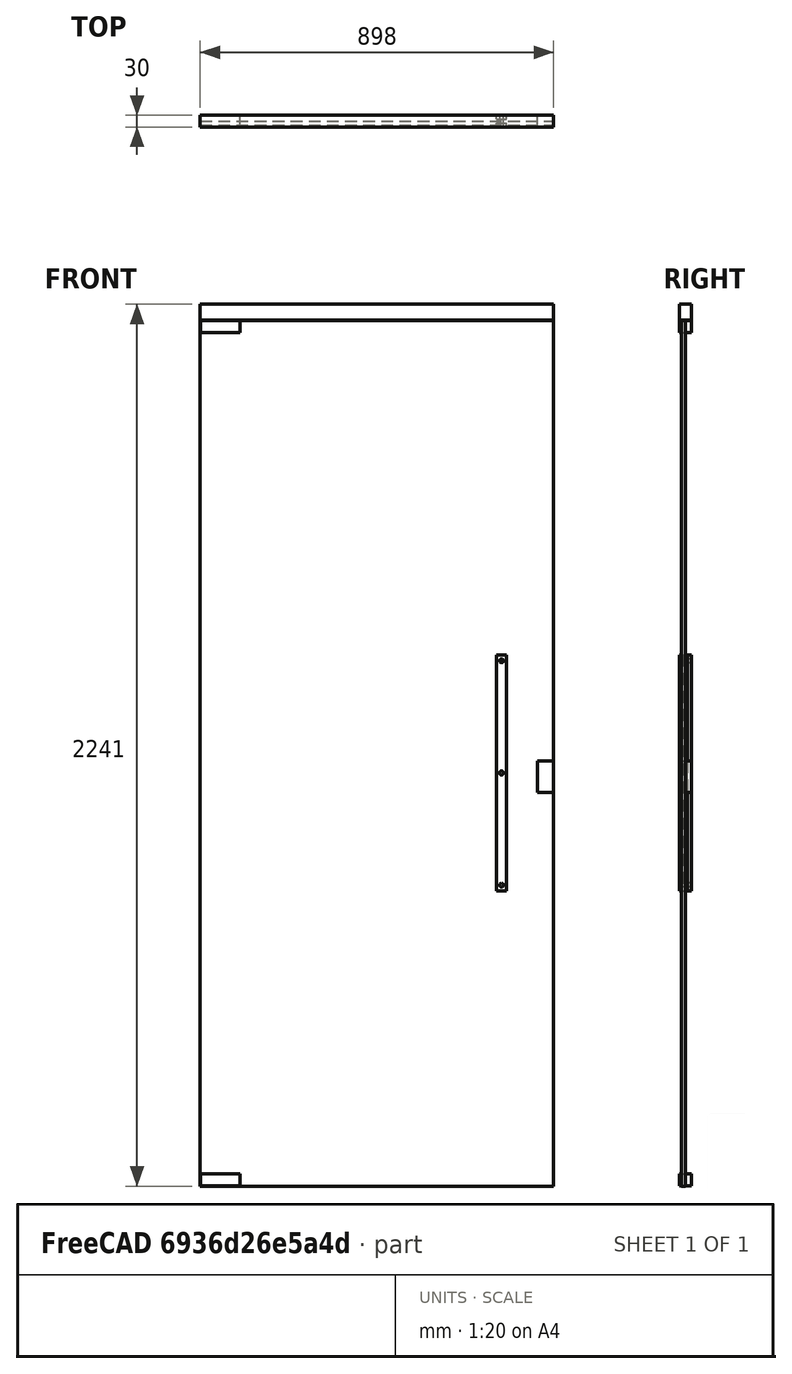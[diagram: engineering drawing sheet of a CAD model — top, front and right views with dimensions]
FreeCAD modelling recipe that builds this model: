
FCSTD DOCUMENT  (FreeCAD 0.16R6704 (Git))
Label: Simple glass door with lintel and handles
License: CreativeCommons Attribution
LicenseURL: http://creativecommons.org/licenses/by/4.0/
objects: Sketcher::SketchObject×2, Part::FeaturePython×1, App::DocumentObjectGroup×1
note: 3 computed .brp shape members not serialized (recipe doc carries the construction recipe); baked Part::Feature solids carry a one-line shape summary decoded from their .brp

FEATURE [Sketcher::SketchObject] Sketch133
  Placement = pos=(0,0,0) rot=(1,0,0;1.5708rad)
  sketch-geometry (37):
    g0: LineSegment StartX=0 StartY=0 StartZ=0 EndX=900 EndY=0 EndZ=0
    g1: LineSegment StartX=900 StartY=2242 StartZ=0 EndX=0 EndY=2242 EndZ=0
    g2: LineSegment StartX=0 StartY=2242 StartZ=0 EndX=0 EndY=0 EndZ=0
    g3: LineSegment StartX=1 StartY=0 StartZ=0 EndX=899 EndY=0 EndZ=0
    g4: LineSegment StartX=899 StartY=0 StartZ=0 EndX=899 EndY=2200 EndZ=0
    g5: LineSegment StartX=899 StartY=2200 StartZ=0 EndX=1 EndY=2200 EndZ=0
    g6: LineSegment StartX=1 StartY=2200 StartZ=0 EndX=1 EndY=0 EndZ=0
    g7: LineSegment StartX=2 StartY=2199 StartZ=0 EndX=102 EndY=2199 EndZ=0
    g8: LineSegment StartX=102 StartY=2199 StartZ=0 EndX=102 EndY=2169 EndZ=0
    g9: LineSegment StartX=102 StartY=2169 StartZ=0 EndX=2 EndY=2169 EndZ=0
    g10: LineSegment StartX=2 StartY=2169 StartZ=0 EndX=2 EndY=2199 EndZ=0
    g11: LineSegment StartX=2 StartY=1 StartZ=0 EndX=102 EndY=1 EndZ=0
    g12: LineSegment StartX=102 StartY=1 StartZ=0 EndX=102 EndY=31 EndZ=0
    g13: LineSegment StartX=102 StartY=31 StartZ=0 EndX=2 EndY=31 EndZ=0
    g14: LineSegment StartX=2 StartY=31 StartZ=0 EndX=2 EndY=1 EndZ=0
    g15: LineSegment StartX=858 StartY=1080 StartZ=0 EndX=898 EndY=1080 EndZ=0
    g16: LineSegment StartX=898 StartY=1080 StartZ=0 EndX=898 EndY=1000 EndZ=0
    g17: LineSegment StartX=898 StartY=1000 StartZ=0 EndX=858 EndY=1000 EndZ=0
    g18: LineSegment StartX=858 StartY=1000 StartZ=0 EndX=858 EndY=1080 EndZ=0
    g19: LineSegment StartX=754 StartY=1350 StartZ=0 EndX=779 EndY=1350 EndZ=0
    g20: LineSegment StartX=779 StartY=1350 StartZ=0 EndX=779 EndY=750 EndZ=0
    g21: LineSegment StartX=779 StartY=750 StartZ=0 EndX=754 EndY=750 EndZ=0
    g22: LineSegment StartX=754 StartY=750 StartZ=0 EndX=754 EndY=1350 EndZ=0
    g23: LineSegment [constr] StartX=766.5 StartY=1473.28 StartZ=0 EndX=766.5 EndY=706.642 EndZ=0
    g24: Circle CenterX=766.5 CenterY=1335 CenterZ=0 NormalX=0 NormalY=0 NormalZ=1 Radius=5
    g25: Circle CenterX=766.5 CenterY=1050 CenterZ=0 NormalX=0 NormalY=0 NormalZ=1 Radius=5
    g26: Circle CenterX=766.5 CenterY=765 CenterZ=0 NormalX=0 NormalY=0 NormalZ=1 Radius=5
    g27: LineSegment [constr] StartX=712 StartY=1050 StartZ=0 EndX=790 EndY=1050 EndZ=0
    g28: LineSegment StartX=900 StartY=2242 StartZ=0 EndX=900 EndY=0 EndZ=0
    g29: LineSegment StartX=-0.1 StartY=2243 StartZ=0 EndX=901 EndY=2243 EndZ=0
    g30: LineSegment StartX=901 StartY=2243 StartZ=0 EndX=901 EndY=0 EndZ=0
    g31: LineSegment StartX=901 StartY=0 StartZ=0 EndX=-0.1 EndY=0 EndZ=0
    g32: LineSegment StartX=-0.1 StartY=0 StartZ=0 EndX=-0.1 EndY=2243 EndZ=0
    g33: LineSegment StartX=1 StartY=2241 StartZ=0 EndX=899 EndY=2241 EndZ=0
    g34: LineSegment StartX=899 StartY=2241 StartZ=0 EndX=899 EndY=2201 EndZ=0
    g35: LineSegment StartX=899 StartY=2201 StartZ=0 EndX=1 EndY=2201 EndZ=0
    g36: LineSegment StartX=1 StartY=2201 StartZ=0 EndX=1 EndY=2241 EndZ=0
  constraints (107):
    c: Coincident(g1,g2)
    c: Coincident(g2,g0)
    c: Horizontal(g0)
    c: Horizontal(g1)
    c: Vertical(g2)
    c: Coincident(g3,g4)
    c: Coincident(g4,g5)
    c: Coincident(g5,g6)
    c: Coincident(g6,g3)
    c: Horizontal(g3)
    c: Horizontal(g5)
    c: Vertical(g4)
    c: Vertical(g6)
    c: DistanceX(g0) = 900  'Largura do vão'
    c: DistanceX(g1,g5) = 1
    c: DistanceX(g3,g0) = 1
    c: DistanceY(g0,g3) = 0
    c: Coincident(g0,g-1)
    c: Coincident(g7,g8)
    c: Coincident(g8,g9)
    c: Coincident(g9,g10)
    c: Coincident(g10,g7)
    c: Horizontal(g7)
    c: Horizontal(g9)
    c: Vertical(g8)
    c: Vertical(g10)
    c: Coincident(g11,g12)
    c: Coincident(g12,g13)
    c: Coincident(g13,g14)
    c: Coincident(g14,g11)
    c: Horizontal(g11)
    c: Horizontal(g13)
    c: Vertical(g12)
    c: Vertical(g14)
    c: Coincident(g15,g16)
    c: Coincident(g16,g17)
    c: Coincident(g17,g18)
    c: Coincident(g18,g15)
    c: Horizontal(g15)
    c: Horizontal(g17)
    c: Vertical(g16)
    c: Vertical(g18)
    c: DistanceX(g5,g7) = 1
    c: DistanceY(g8,g7) = 30  'Altura do apoio'
    c: DistanceX(g9,g8) = 100  'Largura do apoio'
    c: Equal(g8,g12)
    c: Equal(g13,g7)
    c: DistanceX(g3,g11) = 1
    c: DistanceY(g3,g11) = 1
    c: DistanceX(g16,g3) = 1
    c: DistanceY(g17,g15) = 80  'Altura da tranca'
    c: DistanceX(g15,g15) = 40  'Largura da tranca'
    c: DistanceY(g3,g17) = 1000  'Altura da tranca ao chão'
    c: Coincident(g19,g20)
    c: Coincident(g20,g21)
    c: Coincident(g21,g22)
    c: Coincident(g22,g19)
    c: Horizontal(g19)
    c: Horizontal(g21)
    c: Vertical(g20)
    c: Vertical(g22)
    c: DistanceX(g19,g19) = 25  'Largura puxador'
    c: DistanceY(g20,g19) = 600  'Altura do puxador'
    c: Vertical(g23)  'Constraint69'
    c: Symmetric(g19,g19,g23)  'Constraint68'
    c: PointOnObject(g24,g23)  'Constraint72'
    c: PointOnObject(g25,g23)  'Constraint71'
    c: PointOnObject(g26,g23)  'Constraint70'
    c: Radius(g26) = 5  'Apoio puxador'
    c: Equal(g26,g25)  'Constraint83'
    c: Equal(g26,g24)  'Constraint82'
    c: DistanceY(g24,g19) = 15  'Constraint73'
    c: DistanceY(g20,g26) = 15
    c: Horizontal(g27)
    c: PointOnObject(g25,g27)
    c: Symmetric(g21,g19,g27)
    c: DistanceY(g3,g20) = 750  'Distância do puxador ao solo'
    c: DistanceX(g20,g3) = 120  'Distância do puxador'
    c: Coincident(g28,g1)  'Constraint79'
    c: Coincident(g28,g0)
    c: Vertical(g28)
    c: DistanceY(g-1,g5) = 2200  'Altura da porta'
    c: Coincident(g29,g30)  'Constraint93'
    c: Coincident(g30,g31)  'Constraint92'
    c: Coincident(g31,g32)  'Constraint91'
    c: Coincident(g32,g29)
    c: Horizontal(g29)
    c: Horizontal(g31)
    c: Vertical(g30)
    c: Vertical(g32)
    c: DistanceX(g29,g1) = 0.1
    c: DistanceY(g1,g29) = 1
    c: DistanceX(g1,g29) = 1
    c: DistanceY(g31,g-1) = 0  'Constraint117'
    c: Coincident(g33,g34)  'Constraint97'
    c: Coincident(g34,g35)
    c: Coincident(g35,g36)
    c: Coincident(g36,g33)
    c: Horizontal(g33)
    c: Horizontal(g35)
    c: Vertical(g34)
    c: Vertical(g36)
    c: DistanceY(g5,g35) = 1
    c: DistanceY(g33,g1) = 1
    c: DistanceY(g35,g33) = 40  'Altura perfil bandeira'
    c: DistanceX(g34,g4) = 0
    c: DistanceY(g7,g5) = 1
FEATURE [Part::FeaturePython] Window094  label="Simple glass door with lintel and handles 001"  # WARN: FeaturePython — macro-defined, semantics opaque (R4)
  Base = -> Sketch133
  Height = 2100
  HoleDepth = 0
  MoveWithHost = true
  Normal = (0,1,0)
  Preset = 6
  Role = 1
  Width = 900
  WindowParts = PORTA DE VIDRO | Glass panel | Wire1 | 10.0 | 5.0 | APOIO | Frame | Wire2 | 30.0 | 0.0 | APOIO INFERIOR | Frame | Wire3 | 30.0 | 0.0 | TRANCA | Frame | Wire4 | 30.0 | 0.0 | PUXADOR 1 | Frame | Wire5 | 10.0 | 0.0 | PUXADOR 2 | Frame | Wire5 | 10.0 | 20.0 | APOIO SUPERIOR PUXADOR | Frame | Wire6 | 30.0 | 0.0 | APOIO CENTRAL PUXADOR | Frame | Wire7 | 30.0 | 0.0 | APOIO INFERIOR PUXADOR | Frame | Wire8 | 30.0 | 0.0 | PERFIL BANDEIRA | Frame | Wire10 | 30.0 | 0.0
FEATURE [Sketcher::SketchObject] Sketch134  label="Opening indication"
  ExternalGeometry = -> [Window094]
  Placement = pos=(0,5,0) rot=(1,0,0;1.5708rad)
  Support = -> Window094 [Face5]
  sketch-geometry (6):
    g0: LineSegment [constr] StartX=-528.499 StartY=1038.78 StartZ=0 EndX=1595.51 EndY=1038.78 EndZ=0
    g1: LineSegment StartX=56 StartY=2200 StartZ=0 EndX=1 EndY=1038.78 EndZ=0
    g2: LineSegment StartX=1 StartY=1038.78 StartZ=0 EndX=56 EndY=0 EndZ=0
    g3: LineSegment StartX=56 StartY=0 StartZ=0 EndX=899 EndY=1037 EndZ=0
    g4: LineSegment StartX=899 StartY=1037 StartZ=0 EndX=56 EndY=2200 EndZ=0
    g5: LineSegment [constr] StartX=56 StartY=2282.82 StartZ=0 EndX=56 EndY=-151.602 EndZ=0
  constraints (15):
    c: Horizontal(g0)
    c: DistanceY(g-6,g0) = 1038.78  'Latch_height'
    c: PointOnObject(g1,g-3)
    c: PointOnObject(g1,g0)
    c: Coincident(g1,g2)
    c: PointOnObject(g2,g-6)
    c: Coincident(g2,g3)
    c: PointOnObject(g3,g-5)
    c: Coincident(g3,g4)
    c: Coincident(g4,g1)
    c: Vertical(g5)
    c: PointOnObject(g2,g5)
    c: PointOnObject(g1,g5)
    c: PointOnObject(g1,g-4)
    c: DistanceX(g-6,g5) = 55  'Door_axis'
FEATURE [App::DocumentObjectGroup] Grupo101  label="Simple glass door with lintel and handles "
  Group = -> [Window094,Sketch134]
